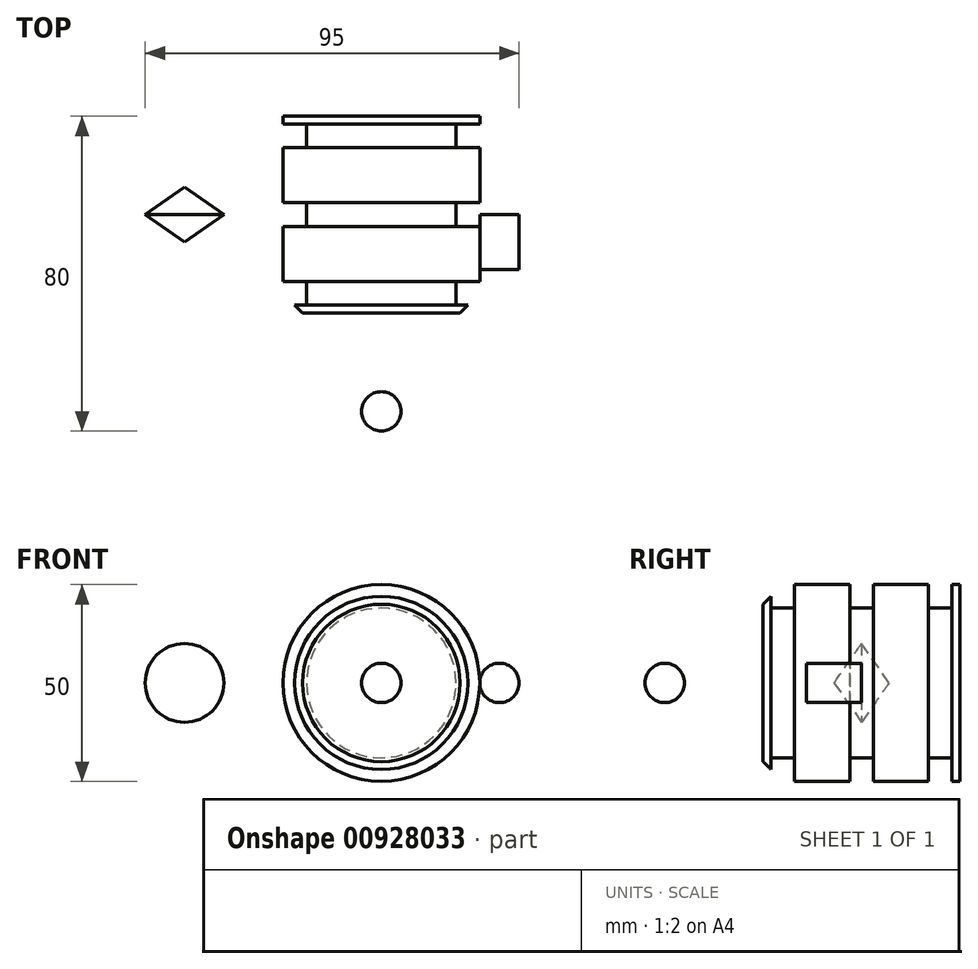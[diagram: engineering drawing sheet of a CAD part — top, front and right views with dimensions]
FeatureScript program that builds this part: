
annotation { "Feature Type Name" : "Feature", "Feature Type Description" : "" }
export const myFeature = defineFeature(function(context is Context, id is Id, definition is map)
    precondition{}
    {
        {
            var Q0;
            Q0=qCreatedBy(makeId("Front.planeOp"),FACE);
            var sketch = newSketch(context, id + "F0", { "sketchPlane" : qUnion([Q0])});
            skCircle(sketch, "E0", {"center": v(0, 0) * mm, "radius": 25 * mm});
            skSolve(sketch);
        }
        {
            var Q0;
            Q0 = qSketchRegion(id + "F0", true);
            extrude(context, id + "F1", {"entities" : qUnion([Q0]), "endBound" : BoundingType.SYMMETRIC, "depth" : 50 * mm, "offsetDistance" : 25 * mm});
        }
        {
            var Q0;
            Q0=qCreatedBy(makeId("Top.planeOp"),FACE);
            var sketch = newSketch(context, id + "F2", { "sketchPlane" : qUnion([Q0])});
            skLineSegment(sketch, "E1.bottom", {"start": v(0, -25) * mm, "end": v(25, -25) * mm});
            skLineSegment(sketch, "E1.top", {"start": v(0, 25) * mm, "end": v(25, 25) * mm});
            skLineSegment(sketch, "E1.left", {"start": v(0, -25) * mm, "end": v(0, 25) * mm});
            skLineSegment(sketch, "E1.right", {"start": v(25, -25) * mm, "end": v(25, -23) * mm});
            skLineSegment(sketch, "E2", {"start": v(25, 23) * mm, "end": v(19, 23) * mm});
            skLineSegment(sketch, "E3", {"start": v(19, 23) * mm, "end": v(19, 17) * mm});
            skLineSegment(sketch, "E4", {"start": v(19, 17) * mm, "end": v(25, 17) * mm});
            skLineSegment(sketch, "E5.1.0.0", {"start": v(25, 3) * mm, "end": v(19, 3) * mm});
            skLineSegment(sketch, "E5.1.0.1", {"start": v(19, 3) * mm, "end": v(19, -3) * mm});
            skLineSegment(sketch, "E5.1.0.2", {"start": v(19, -3) * mm, "end": v(25, -3) * mm});
            skLineSegment(sketch, "E5.2.0.0", {"start": v(25, -17) * mm, "end": v(19, -17) * mm});
            skLineSegment(sketch, "E5.2.0.1", {"start": v(19, -17) * mm, "end": v(19, -23) * mm});
            skLineSegment(sketch, "E5.2.0.2", {"start": v(19, -23) * mm, "end": v(25, -23) * mm});
            skLineSegment(sketch, "E5.direction1", {"start": v(19, 23) * mm, "end": v(19, 3) * mm, "construction": true});
            skLineSegment(sketch, "E6.trimOffspring", {"start": v(25, 23) * mm, "end": v(25, 25) * mm});
            skLineSegment(sketch, "E7.trimOffspring", {"start": v(25, 3) * mm, "end": v(25, 17) * mm});
            skLineSegment(sketch, "E8.trimOffspring", {"start": v(25, -17) * mm, "end": v(25, -3) * mm});
            skSolve(sketch);
        }
        {
            var Q0;
            Q0 = qSketchRegion(id + "F2", true);
            var Q1;
            Q1=sQuery(id+"F2.wireOp",EDGE,"E1.left");
            revolve(context, id + "F3", {"surfaceOperationType" : NewSurfaceOperationType.NEW, "entities" : qUnion([Q0]), "axis" : qUnion([Q1]), "revolveType" : RevolveType.FULL});
        }
        {
            var Q0;
            Q0=makeQuery(id+"F1.opExtrude","SWEPT_BODY",BODY,{"disambiguationData":[OSD([sQuery(id+"F0.wireOp",EDGE,"E0")])]});
            deleteBodies(context, id + "F4", {"entities" : qUnion([Q0])});
        }
        {
            var Q0;
            Q0=qCreatedBy(makeId("Front.planeOp"),FACE);
            var sketch = newSketch(context, id + "F5", { "sketchPlane" : qUnion([Q0])});
            skCircle(sketch, "E9", {"center": v(30, 0) * mm, "radius": 5 * mm});
            skSolve(sketch);
        }
        {
            var Q0;
            Q0 = qSketchRegion(id + "F5", true);
            extrude(context, id + "F6", {"entities" : qUnion([Q0]), "depth" : 14 * mm, "offsetDistance" : 25 * mm});
        }
        {
            var Q0;
            Q0=qCreatedBy(makeId("Top.planeOp"),FACE);
            var sketch = newSketch(context, id + "F7", { "sketchPlane" : qUnion([Q0])});
            skArc(sketch, "E10", {"start": v(0, -45) * mm, "mid": v(5, -50) * mm, "end": v(0, -55) * mm});
            skLineSegment(sketch, "E11", {"start": v(0, -55) * mm, "end": v(0, -45) * mm});
            skSolve(sketch);
        }
        {
            var Q0;
            Q0 = qSketchRegion(id + "F7", true);
            var Q1;
            Q1=sQuery(id+"F7.wireOp",EDGE,"E11");
            revolve(context, id + "F8", {"surfaceOperationType" : NewSurfaceOperationType.NEW, "entities" : qUnion([Q0]), "axis" : qUnion([Q1]), "revolveType" : RevolveType.FULL});
        }
        {
            var Q0;
            Q0=makeQuery(id+"F3.opRevolve","SWEPT_EDGE",EDGE,{"disambiguationData":[OSD([sQuery(id+"F2.wireOp",EDGE,"E1.bottom"),sQuery(id+"F2.wireOp",EDGE,"E1.right")])]});
            chamfer(context, id + "F9", {"entities" : qUnion([Q0]), "width" : 5 * mm, "tangentPropagation" : true});
        }
        {
            var Q0;
            Q0=qCreatedBy(makeId("Top.planeOp"),FACE);
            var sketch = newSketch(context, id + "F10", { "sketchPlane" : qUnion([Q0])});
            skLineSegment(sketch, "E12", {"start": v(-50, 0) * mm, "end": v(-50, -7) * mm});
            skLineSegment(sketch, "E13", {"start": v(-50, -7) * mm, "end": v(-40, 0) * mm});
            skLineSegment(sketch, "E14.MirrorCS", {"start": v(-50, 0) * mm, "end": v(-50, 7) * mm});
            skLineSegment(sketch, "E15.MirrorCS", {"start": v(-50, 7) * mm, "end": v(-40, 0) * mm});
            skSolve(sketch);
        }
        {
            var Q0;
            Q0 = qSketchRegion(id + "F10", true);
            var Q1;
            Q1=sQuery(id+"F10.wireOp",EDGE,"E12");
            revolve(context, id + "F11", {"surfaceOperationType" : NewSurfaceOperationType.NEW, "entities" : qUnion([Q0]), "axis" : qUnion([Q1]), "revolveType" : RevolveType.FULL});
        }
    });
